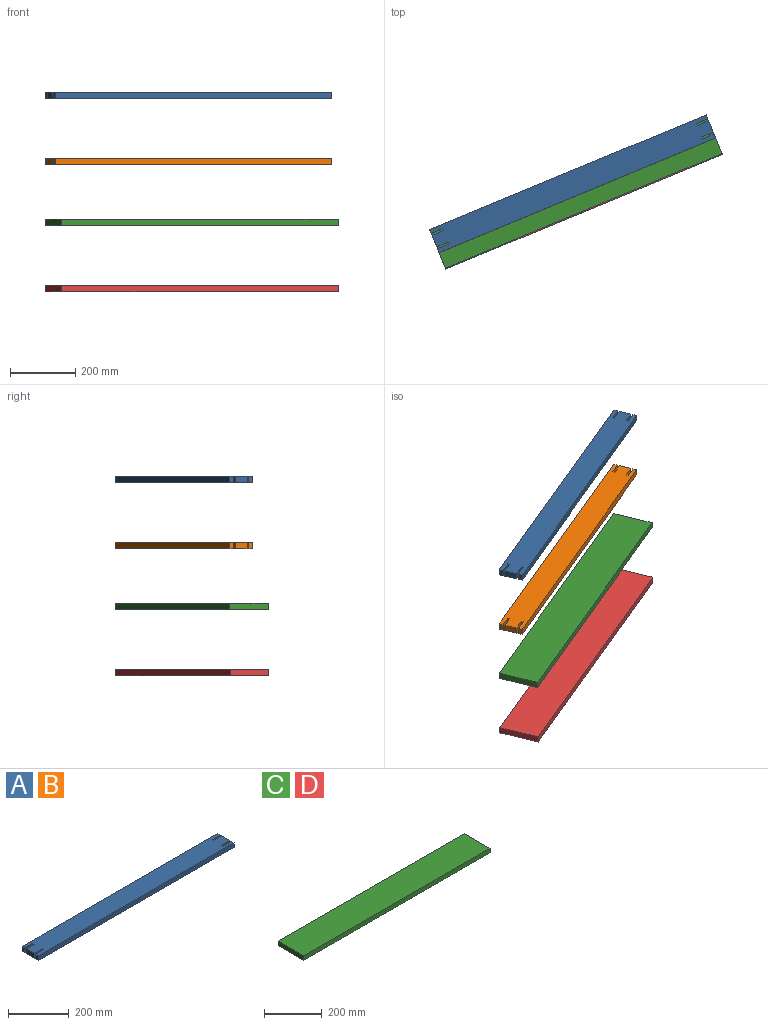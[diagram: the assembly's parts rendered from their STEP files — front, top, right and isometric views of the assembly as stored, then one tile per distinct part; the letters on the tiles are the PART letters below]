
ASSEMBLY  parts=4 mates=4
PART A: 22 faces, bbox 914.4x76.2x19.1 mm
  f0: plane 19.05x12.7mm, normal (-1,0,0), area 241.9mm2, adj f4,f5,f9,f15
  f1: plane 38.1x19.05mm, normal (-1,0,0), area 725.8mm2, adj f4,f5,f11,f13
  f2: plane 38.1x19.05mm, normal (1,0,0), area 725.8mm2, adj f4,f5,f17,f19
  f3: plane 19.05x12.7mm, normal (1,0,0), area 241.9mm2, adj f4,f5,f9,f16
  f4: plane 914.4x76.2mm, normal (0,0,1), area 68709.5mm2, adj f0,f1,f2,f3,f6,f7,f8,f9
  f5: plane 914.4x76.2mm, normal (0,0,-1), area 68709.5mm2, adj f0,f1,f2,f3,f6,f7,f8,f9
  f6: plane 19.05x12.7mm, normal (-1,0,0), area 241.9mm2, adj f4,f5,f7,f10
  f7: plane 914.4x19.05mm, normal (0,-1,0), area 17419.3mm2, adj f4,f5,f6,f8
  f8: plane 19.05x12.7mm, normal (1,0,0), area 241.9mm2, adj f4,f5,f7,f21
  f9: plane 914.4x19.05mm, normal (0,1,0), area 17419.3mm2, adj f0,f3,f4,f5
  f10: plane 38.1x19.05mm, normal (0,1,0), area 725.8mm2, adj f4,f5,f6,f12
  f11: plane 38.1x19.05mm, normal (0,-1,0), area 725.8mm2, adj f1,f4,f5,f12
  f12: plane 19.05x6.35mm, normal (-1,0,0), area 121mm2, adj f4,f5,f10,f11
  f13: plane 38.1x19.05mm, normal (0,1,0), area 725.8mm2, adj f1,f4,f5,f14
  f14: plane 19.05x6.35mm, normal (-1,0,0), area 121mm2, adj f4,f5,f13,f15
  f15: plane 38.1x19.05mm, normal (0,-1,0), area 725.8mm2, adj f0,f4,f5,f14
  f16: plane 38.1x19.05mm, normal (0,-1,0), area 725.8mm2, adj f3,f4,f5,f18
  f17: plane 38.1x19.05mm, normal (0,1,0), area 725.8mm2, adj f2,f4,f5,f18
  f18: plane 19.05x6.35mm, normal (1,0,0), area 121mm2, adj f4,f5,f16,f17
  f19: plane 38.1x19.05mm, normal (0,-1,0), area 725.8mm2, adj f2,f4,f5,f20
  f20: plane 19.05x6.35mm, normal (1,0,0), area 121mm2, adj f4,f5,f19,f21
  f21: plane 38.1x19.05mm, normal (0,1,0), area 725.8mm2, adj f4,f5,f8,f20
PART B: same geometry as A
PART C: 6 faces, bbox 914.4x127x19.1 mm
  f0: plane 127x19.05mm, normal (-1,0,0), area 2419.3mm2, adj f1,f3,f4,f5
  f1: plane 914.4x19.05mm, normal (0,-1,0), area 17419.3mm2, adj f0,f2,f4,f5
  f2: plane 127x19.05mm, normal (1,0,0), area 2419.3mm2, adj f1,f3,f4,f5
  f3: plane 914.4x19.05mm, normal (0,1,0), area 17419.3mm2, adj f0,f2,f4,f5
  f4: plane 914.4x127mm, normal (0,0,1), area 116128.8mm2, adj f0,f1,f2,f3
  f5: plane 914.4x127mm, normal (0,0,-1), area 116128.8mm2, adj f0,f1,f2,f3
PART D: same geometry as C
PLACE A rot(axis=(0,0,1),22.5deg) t=(3.89,28.71,548.89)mm
PLACE B rot(axis=(0,0,-1),157.5deg) t=(-25.3,99.1,345.69)mm
PLACE C rot(axis=(0.2,-0.98,0),180deg) t=(23.35,-18.21,180.59)mm
PLACE D rot(axis=(0,0,1),22.5deg) t=(24.32,-20.56,-41.66)mm
MATE parallel C.f4 <-> B.f4  axis (0,0,-1) through (-0.97,40.45,161.54)mm
MATE parallel A.f4 <-> B.f4  axis (0,0,1) through (-10.7,63.91,567.94)mm
MATE parallel D.f5 <-> C.f4  axis (0,0,-1) through (0,38.1,-41.66)mm
MATE parallel B.f7 <-> C.f3  axis (-0.38,0.92,0) through (-25.3,99.1,355.22)mm
